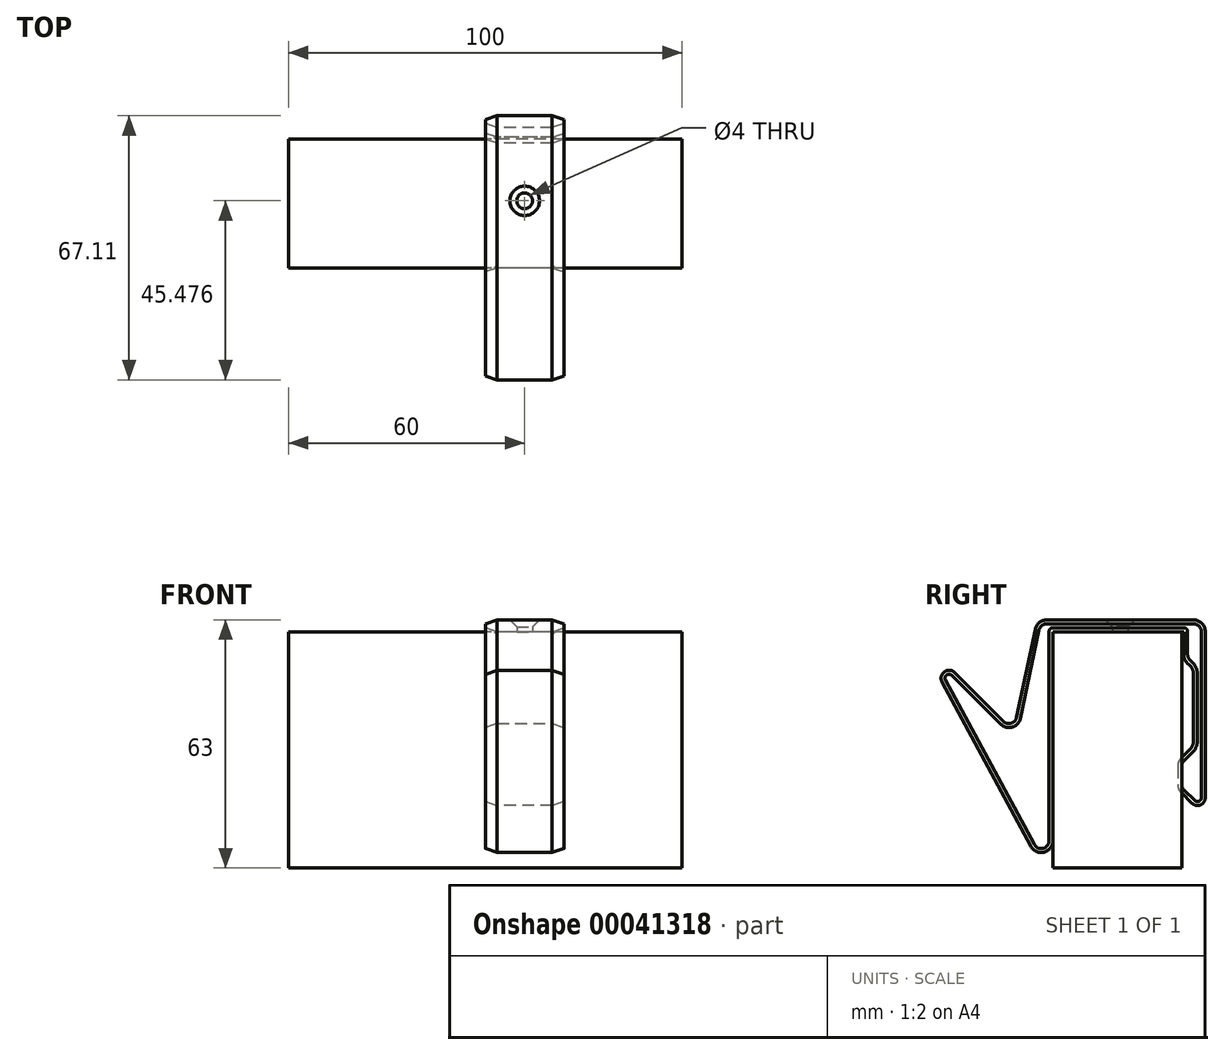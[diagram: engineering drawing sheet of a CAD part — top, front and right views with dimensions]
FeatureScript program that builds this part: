
annotation { "Feature Type Name" : "Feature", "Feature Type Description" : "" }
export const myFeature = defineFeature(function(context is Context, id is Id, definition is map)
    precondition{}
    {
        {
            var Q0;
            Q0=qCreatedBy(makeId("Right.planeOp"),FACE);
            var sketch = newSketch(context, id + "F0", { "sketchPlane" : qUnion([Q0])});
            skLineSegment(sketch, "E0.bottom", {"start": v(0, 0) * mm, "end": v(32.7, 0) * mm});
            skLineSegment(sketch, "E0.top", {"start": v(0, -60) * mm, "end": v(32.7, -60) * mm});
            skLineSegment(sketch, "E0.left", {"start": v(0, 0) * mm, "end": v(0, -60) * mm});
            skLineSegment(sketch, "E0.right", {"start": v(32.7, 0) * mm, "end": v(32.7, -60) * mm});
            skSolve(sketch);
        }
        {
            var Q0;
            Q0 = qSketchRegion(id + "F0", true);
            extrude(context, id + "F1", {"entities" : qUnion([Q0]), "depth" : 50 * mm, "hasSecondDirection" : true, "secondDirectionOppositeDirection" : true, "secondDirectionDepth" : 50 * mm});
        }
        {
            var Q0;
            Q0=qCreatedBy(makeId("Right.planeOp"),FACE);
            var sketch = newSketch(context, id + "F2", { "sketchPlane" : qUnion([Q0])});
            skLineSegment(sketch, "E1", {"start": v(0, -65) * mm, "end": v(-28.17, -12.75) * mm});
            skLineSegment(sketch, "E2", {"start": v(-25, -10.38) * mm, "end": v(-10, -25.38) * mm});
            skLineSegment(sketch, "E3", {"start": v(-10, -25.38) * mm, "end": v(-4, 3) * mm});
            skLineSegment(sketch, "E4", {"start": v(-4, 3) * mm, "end": v(38.7, 3) * mm});
            skLineSegment(sketch, "E5", {"start": v(38.7, 3) * mm, "end": v(38.7, -47) * mm});
            skLineSegment(sketch, "E6", {"start": v(38.7, -47) * mm, "end": v(31.7, -40) * mm});
            skLineSegment(sketch, "E7", {"start": v(31.7, -40) * mm, "end": v(31.7, -33) * mm});
            skLineSegment(sketch, "E8", {"start": v(31.7, -33) * mm, "end": v(35.7, -29) * mm});
            skLineSegment(sketch, "E9", {"start": v(35.7, -29) * mm, "end": v(35.7, -9.5) * mm});
            skLineSegment(sketch, "E10", {"start": v(35.7, -9.5) * mm, "end": v(33.2, -7) * mm});
            skLineSegment(sketch, "E11", {"start": v(33.2, -7) * mm, "end": v(33.2, 0) * mm});
            skLineSegment(sketch, "E12", {"start": v(33.2, 0) * mm, "end": v(0, 0) * mm});
            skLineSegment(sketch, "E13", {"start": v(0, 0) * mm, "end": v(0, -65) * mm});
            skArc(sketch, "E14", {"start": v(-25, -10.38) * mm, "mid": v(-27.6, -10.2) * mm, "end": v(-28.17, -12.75) * mm});
            skSolve(sketch);
        }
        {
            var Q0;
            Q0 = qSketchRegion(id + "F2", true);
            extrude(context, id + "F3", {"entities" : qUnion([Q0]), "depth" : 20 * mm});
        }
        {
            var Q0;
            Q0=makeQuery(id+"F3.opExtrude","SWEPT_EDGE",EDGE,{"disambiguationData":[OSD([sQuery(id+"F2.wireOp",EDGE,"E1"),sQuery(id+"F2.wireOp",EDGE,"E13")])]});
            fillet(context, id + "F4", {"entities" : qUnion([Q0]), "radius" : 3 * mm, "tangentPropagation" : true, "allowEdgeOverflow" : false});
        }
        {
            var Q0;
            Q0=makeQuery(id+"F3.opExtrude","SWEPT_EDGE",EDGE,{"disambiguationData":[OSD([sQuery(id+"F2.wireOp",EDGE,"E2"),sQuery(id+"F2.wireOp",EDGE,"E3")])]});
            fillet(context, id + "F5", {"entities" : qUnion([Q0]), "radius" : 2 * mm, "tangentPropagation" : true, "allowEdgeOverflow" : false});
        }
        {
            var Q0;
            Q0=makeQuery(id+"F3.opExtrude","SWEPT_EDGE",EDGE,{"disambiguationData":[OSD([sQuery(id+"F2.wireOp",EDGE,"E3"),sQuery(id+"F2.wireOp",EDGE,"E4")])]});
            var Q1;
            Q1=makeQuery(id+"F3.opExtrude","SWEPT_EDGE",EDGE,{"disambiguationData":[OSD([sQuery(id+"F2.wireOp",EDGE,"E4"),sQuery(id+"F2.wireOp",EDGE,"E5")])]});
            fillet(context, id + "F6", {"entities" : qUnion([Q0, Q1]), "radius" : 3 * mm, "tangentPropagation" : true, "allowEdgeOverflow" : false});
        }
        {
            var Q0;
            Q0=makeQuery(id+"F3.opExtrude","SWEPT_EDGE",EDGE,{"disambiguationData":[OSD([sQuery(id+"F2.wireOp",EDGE,"E5"),sQuery(id+"F2.wireOp",EDGE,"E6")])]});
            fillet(context, id + "F7", {"entities" : qUnion([Q0]), "radius" : 2 * mm, "tangentPropagation" : true, "allowEdgeOverflow" : false});
        }
        {
            var Q0;
            Q0=makeQuery(id+"F3.opExtrude","SWEPT_EDGE",EDGE,{"disambiguationData":[OSD([sQuery(id+"F2.wireOp",EDGE,"E10"),sQuery(id+"F2.wireOp",EDGE,"E11")])]});
            var Q1;
            Q1=makeQuery(id+"F3.opExtrude","SWEPT_EDGE",EDGE,{"disambiguationData":[OSD([sQuery(id+"F2.wireOp",EDGE,"E9"),sQuery(id+"F2.wireOp",EDGE,"E10")])]});
            var Q2;
            Q2=makeQuery(id+"F3.opExtrude","SWEPT_EDGE",EDGE,{"disambiguationData":[OSD([sQuery(id+"F2.wireOp",EDGE,"E8"),sQuery(id+"F2.wireOp",EDGE,"E9")])]});
            var Q3;
            Q3=makeQuery(id+"F3.opExtrude","SWEPT_EDGE",EDGE,{"disambiguationData":[OSD([sQuery(id+"F2.wireOp",EDGE,"E7"),sQuery(id+"F2.wireOp",EDGE,"E8")])]});
            var Q4;
            Q4=makeQuery(id+"F3.opExtrude","SWEPT_EDGE",EDGE,{"disambiguationData":[OSD([sQuery(id+"F2.wireOp",EDGE,"E6"),sQuery(id+"F2.wireOp",EDGE,"E7")])]});
            fillet(context, id + "F8", {"entities" : qUnion([Q0, Q1, Q2, Q3, Q4]), "radius" : 3 * mm, "tangentPropagation" : true, "allowEdgeOverflow" : false});
        }
        {
            var Q0;
            Q0=makeQuery(id+"F3.opExtrude","CAP_FACE",FACE,{"disambiguationData":[OSD([sQuery(id+"F2.wireOp",EDGE,"E1"),sQuery(id+"F2.wireOp",EDGE,"E2"),sQuery(id+"F2.wireOp",EDGE,"E3"),sQuery(id+"F2.wireOp",EDGE,"E4"),sQuery(id+"F2.wireOp",EDGE,"E5"),sQuery(id+"F2.wireOp",EDGE,"E6"),sQuery(id+"F2.wireOp",EDGE,"E7"),sQuery(id+"F2.wireOp",EDGE,"E8"),sQuery(id+"F2.wireOp",EDGE,"E9"),sQuery(id+"F2.wireOp",EDGE,"E10"),sQuery(id+"F2.wireOp",EDGE,"E11"),sQuery(id+"F2.wireOp",EDGE,"E12"),sQuery(id+"F2.wireOp",EDGE,"E13"),sQuery(id+"F2.wireOp",EDGE,"E14")])],"isStart":false});
            chamfer(context, id + "F9", {"entities" : qUnion([Q0]), "chamferType" : ChamferType.TWO_OFFSETS, "width1" : 3 * mm, "oppositeDirection" : false, "width2" : 1 * mm, "tangentPropagation" : true});
        }
        {
            var Q0;
            Q0=makeQuery(id+"F3.opExtrude","CAP_FACE",FACE,{"disambiguationData":[OSD([sQuery(id+"F2.wireOp",EDGE,"E1"),sQuery(id+"F2.wireOp",EDGE,"E2"),sQuery(id+"F2.wireOp",EDGE,"E3"),sQuery(id+"F2.wireOp",EDGE,"E4"),sQuery(id+"F2.wireOp",EDGE,"E5"),sQuery(id+"F2.wireOp",EDGE,"E6"),sQuery(id+"F2.wireOp",EDGE,"E7"),sQuery(id+"F2.wireOp",EDGE,"E8"),sQuery(id+"F2.wireOp",EDGE,"E9"),sQuery(id+"F2.wireOp",EDGE,"E10"),sQuery(id+"F2.wireOp",EDGE,"E11"),sQuery(id+"F2.wireOp",EDGE,"E12"),sQuery(id+"F2.wireOp",EDGE,"E13"),sQuery(id+"F2.wireOp",EDGE,"E14")])],"isStart":true});
            chamfer(context, id + "F10", {"entities" : qUnion([Q0]), "chamferType" : ChamferType.TWO_OFFSETS, "width1" : 1 * mm, "oppositeDirection" : false, "width2" : 3 * mm, "tangentPropagation" : true});
        }
        {
            var Q0;
            Q0=makeQuery(id+"F3.opExtrude","SWEPT_FACE",FACE,{"disambiguationData":[OSD([sQuery(id+"F2.wireOp",EDGE,"E4")])]});
            var sketch = newSketch(context, id + "F11", { "sketchPlane" : qUnion([Q0])});
            skLineSegment(sketch, "E15", {"start": v(3, 35.7) * mm, "end": v(17, -1.57) * mm, "construction": true});
            skLineSegment(sketch, "E16", {"start": v(17, 35.7) * mm, "end": v(3, -1.57) * mm, "construction": true});
            skPoint(sketch, "E17", {"position": v(10, 17.07) * mm});
            skSolve(sketch);
        }
        {
            var Q0;
            Q0=sQuery(id+"F11.wireOp",VERTEX,"E17");
            var Q1;
            Q1=makeQuery(id+"F3.opExtrude","SWEPT_BODY",BODY,{"disambiguationData":[OSD([sQuery(id+"F2.wireOp",EDGE,"E1"),sQuery(id+"F2.wireOp",EDGE,"E2"),sQuery(id+"F2.wireOp",EDGE,"E3"),sQuery(id+"F2.wireOp",EDGE,"E4"),sQuery(id+"F2.wireOp",EDGE,"E5"),sQuery(id+"F2.wireOp",EDGE,"E6"),sQuery(id+"F2.wireOp",EDGE,"E7"),sQuery(id+"F2.wireOp",EDGE,"E8"),sQuery(id+"F2.wireOp",EDGE,"E9"),sQuery(id+"F2.wireOp",EDGE,"E10"),sQuery(id+"F2.wireOp",EDGE,"E11"),sQuery(id+"F2.wireOp",EDGE,"E12"),sQuery(id+"F2.wireOp",EDGE,"E13"),sQuery(id+"F2.wireOp",EDGE,"E14")])]});
            hole(context, id + "F12", {"style" : HoleStyle.C_SINK, "holeDiameter" : 4 * mm, "cSinkDiameter" : 7.5 * mm, "endStyle" : HoleEndStyle.THROUGH, "locations" : qUnion([Q0]), "scope" : qUnion([Q1]), "cSinkAngle" : 90 * degree});
        }
        {
            var Q0;
            Q0=makeQuery(id+"F9.opChamfer","BLEND_EDGE",EDGE,{"blendedFrom":[makeQuery(id+"F3.opExtrude","CAP_EDGE",EDGE,{"disambiguationData":[OSD([sQuery(id+"F2.wireOp",EDGE,"E12")])],"isStart":false}),makeQuery(id+"F3.opExtrude","CAP_EDGE",EDGE,{"disambiguationData":[OSD([sQuery(id+"F2.wireOp",EDGE,"E13")])],"isStart":false})],"blendedInto":[]});
            var Q1;
            Q1=makeQuery(id+"F9.opChamfer","BLEND_EDGE",EDGE,{"blendedFrom":[makeQuery(id+"F3.opExtrude","CAP_EDGE",EDGE,{"disambiguationData":[OSD([sQuery(id+"F2.wireOp",EDGE,"E12")])],"isStart":false}),makeQuery(id+"F3.opExtrude","CAP_EDGE",EDGE,{"disambiguationData":[OSD([sQuery(id+"F2.wireOp",EDGE,"E11")])],"isStart":false})],"blendedInto":[]});
            var Q2;
            Q2=makeQuery(id+"F10.opChamfer","BLEND_EDGE",EDGE,{"blendedFrom":[makeQuery(id+"F3.opExtrude","CAP_EDGE",EDGE,{"disambiguationData":[OSD([sQuery(id+"F2.wireOp",EDGE,"E12")])],"isStart":true}),makeQuery(id+"F3.opExtrude","CAP_EDGE",EDGE,{"disambiguationData":[OSD([sQuery(id+"F2.wireOp",EDGE,"E13")])],"isStart":true})],"blendedInto":[]});
            var Q3;
            Q3=makeQuery(id+"F10.opChamfer","BLEND_EDGE",EDGE,{"blendedFrom":[makeQuery(id+"F3.opExtrude","CAP_EDGE",EDGE,{"disambiguationData":[OSD([sQuery(id+"F2.wireOp",EDGE,"E12")])],"isStart":true}),makeQuery(id+"F3.opExtrude","CAP_EDGE",EDGE,{"disambiguationData":[OSD([sQuery(id+"F2.wireOp",EDGE,"E11")])],"isStart":true})],"blendedInto":[]});
            fillet(context, id + "F13", {"entities" : qUnion([Q0, Q1, Q2, Q3]), "radius" : 1 * mm, "tangentPropagation" : true, "allowEdgeOverflow" : false});
        }
    });
